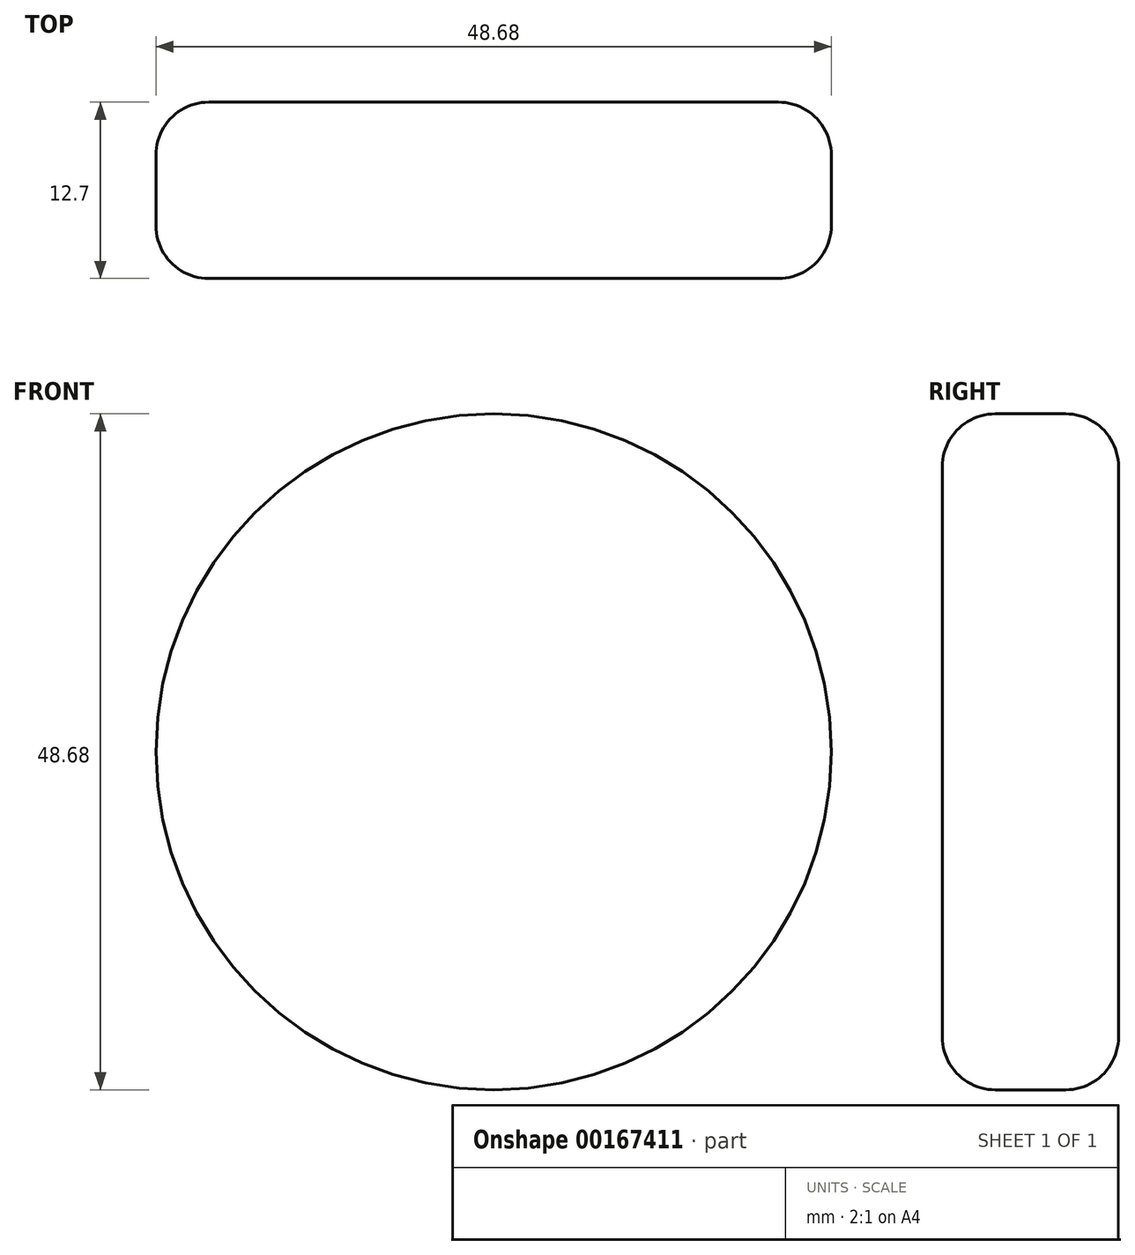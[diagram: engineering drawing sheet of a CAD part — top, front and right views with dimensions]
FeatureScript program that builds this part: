
annotation { "Feature Type Name" : "Feature", "Feature Type Description" : "" }
export const myFeature = defineFeature(function(context is Context, id is Id, definition is map)
    precondition{}
    {
        {
            var Q0;
            Q0=qCreatedBy(makeId("Front.planeOp"),FACE);
            var sketch = newSketch(context, id + "F0", { "sketchPlane" : qUnion([Q0])});
            skCircle(sketch, "E0", {"center": v(0, 0) * mm, "radius": 24.34 * mm});
            skSolve(sketch);
        }
        {
            var Q0;
            Q0=makeQuery(id+"F0.imprint","IMPRINT",FACE,{"disambiguationData":[TD([[makeQuery(id+"F0.imprint","IMPRINT",EDGE,{"derivedFrom":sQuery(id+"F0.wireOp",EDGE,"E0")}),1.0]])]});
            extrude(context, id + "F1", {"entities" : qUnion([Q0]), "depth" : 12.7 * mm});
        }
        {
            var Q0;
            Q0=makeQuery(id+"F1.opExtrude","CAP_EDGE",EDGE,{"disambiguationData":[OSD([sQuery(id+"F0.wireOp",EDGE,"E0")])],"isStart":true});
            var Q1;
            Q1=makeQuery(id+"F1.opExtrude","CAP_EDGE",EDGE,{"disambiguationData":[OSD([sQuery(id+"F0.wireOp",EDGE,"E0")])],"isStart":false});
            fillet(context, id + "F2", {"entities" : qUnion([Q0, Q1]), "radius" : 3.8 * mm, "tangentPropagation" : true, "allowEdgeOverflow" : false});
        }
    });
